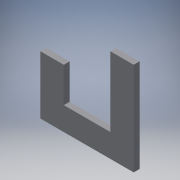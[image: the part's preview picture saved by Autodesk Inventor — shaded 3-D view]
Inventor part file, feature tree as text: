
AUTODESK INVENTOR PART (.ipt)
format: ipt  version: 2016 (Build 200138000, 138)  size: 95,232 bytes
history: native  units: in
note: dims shown in document units (in); Inventor stores cm internally (conversion verified against a paired STEP export)
features: extrude x1, sketch x1
ambient origin geometry x8: Origin, YZ Plane, XZ Plane, XY Plane, X Axis, Y Axis, Z Axis, Center Point
bodies: Solid1 (feature_tree)
feature tree (2):
  extrude  "Extrusion1"  Depth=1.0in
  sketch  "Sketch1"  dims[d0=4.0in d1=1.0in d2=1.0in d3=1.0in d4=2.0in d5=3.0in d6=2.5in d7=0.25in d8=0.0in]
